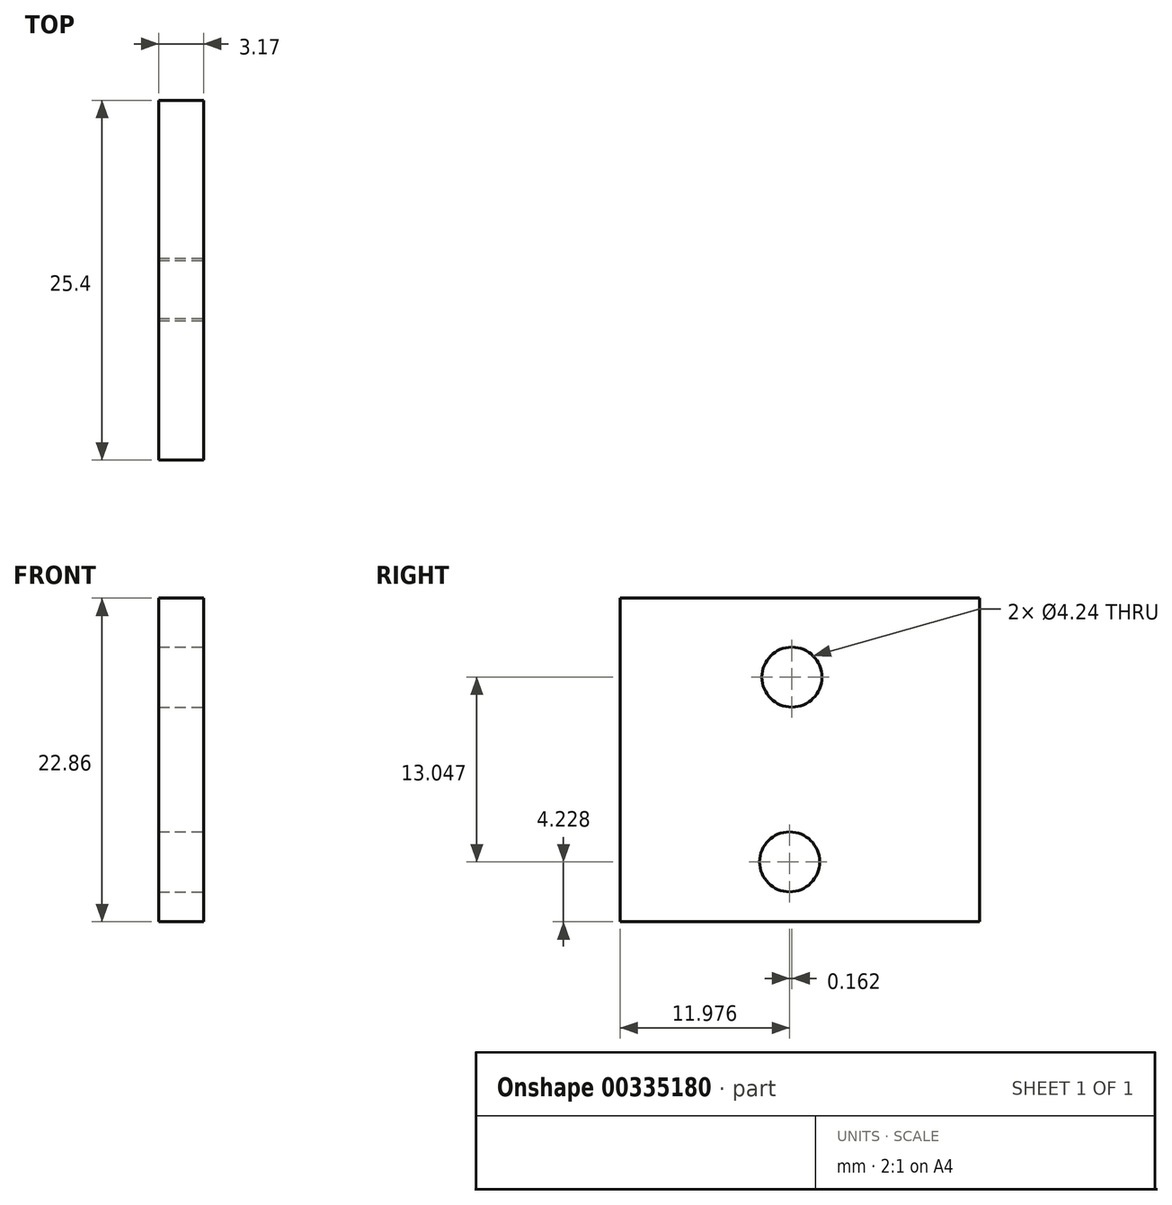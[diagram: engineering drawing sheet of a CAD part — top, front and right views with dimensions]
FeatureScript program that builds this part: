
annotation { "Feature Type Name" : "Feature", "Feature Type Description" : "" }
export const myFeature = defineFeature(function(context is Context, id is Id, definition is map)
    precondition{}
    {
        {
            var Q0;
            Q0=qCreatedBy(makeId("Front.planeOp"),FACE);
            var sketch = newSketch(context, id + "F0", { "sketchPlane" : qUnion([Q0])});
            skLineSegment(sketch, "E0.bottom", {"start": v(-10.5, 7.9) * mm, "end": v(-7.32, 7.9) * mm});
            skLineSegment(sketch, "E0.top", {"start": v(-10.5, -14.95) * mm, "end": v(-7.32, -14.95) * mm});
            skLineSegment(sketch, "E0.left", {"start": v(-10.5, 7.9) * mm, "end": v(-10.5, -14.95) * mm});
            skLineSegment(sketch, "E0.right", {"start": v(-7.32, 7.9) * mm, "end": v(-7.32, -14.95) * mm});
            skSolve(sketch);
        }
        {
            var Q0;
            Q0 = qSketchRegion(id + "F0", true);
            extrude(context, id + "F1", {"entities" : qUnion([Q0]), "depth" : 25.4 * mm});
        }
        {
            var Q0;
            Q0=makeQuery(id+"F1.opExtrude","SWEPT_FACE",FACE,{"disambiguationData":[OSD([sQuery(id+"F0.wireOp",EDGE,"E0.right")])]});
            var sketch = newSketch(context, id + "F2", { "sketchPlane" : qUnion([Q0])});
            skCircle(sketch, "E1", {"center": v(-13.26, 2.32) * mm, "radius": 2.12 * mm});
            skCircle(sketch, "E2", {"center": v(-13.42, -10.72) * mm, "radius": 2.12 * mm});
            skSolve(sketch);
        }
        {
            var Q0;
            Q0 = qSketchRegion(id + "F2", true);
            extrude(context, id + "F3", {"entities" : qUnion([Q0]), "operationType" : NewBodyOperationType.REMOVE, "oppositeDirection" : true, "depth" : 4.24 * mm});
        }
    });
